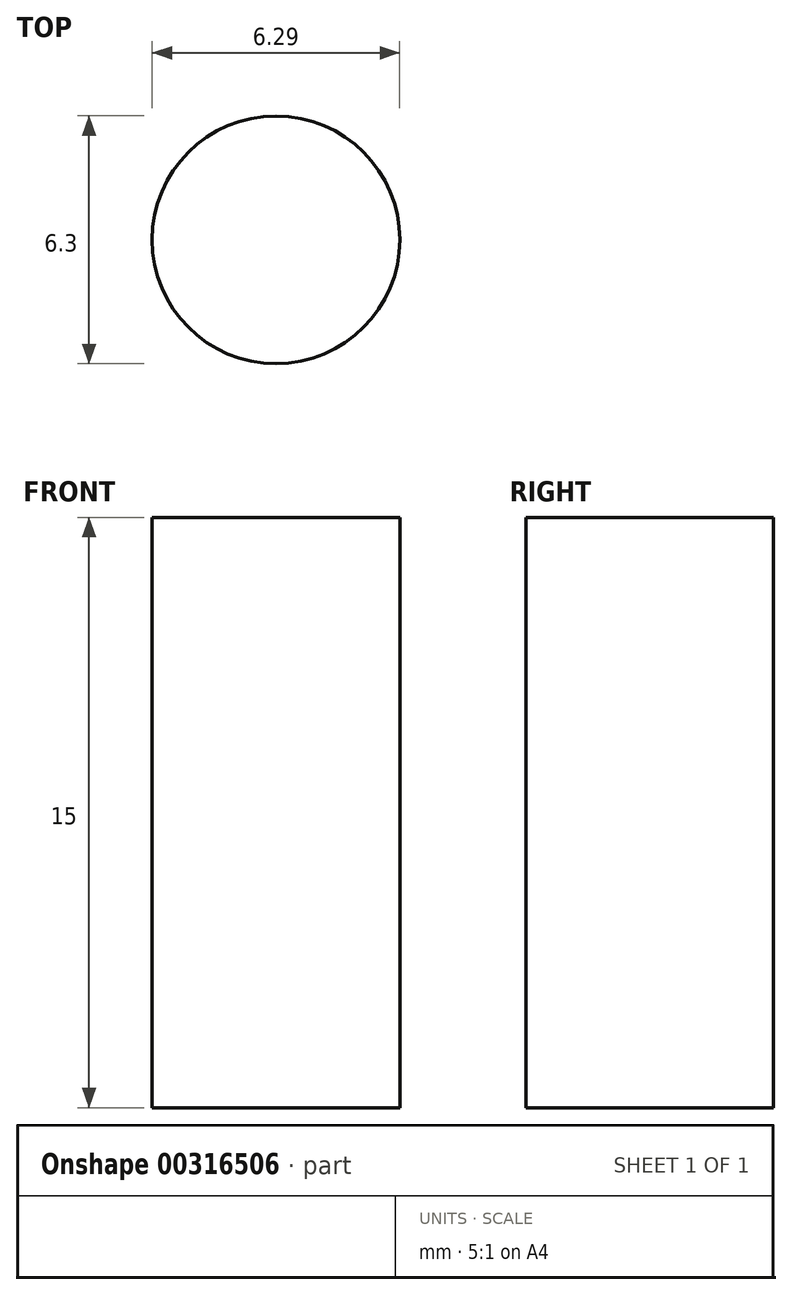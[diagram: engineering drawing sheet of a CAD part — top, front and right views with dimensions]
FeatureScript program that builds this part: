
annotation { "Feature Type Name" : "Feature", "Feature Type Description" : "" }
export const myFeature = defineFeature(function(context is Context, id is Id, definition is map)
    precondition{}
    {
        {
            var Q0;
            Q0=qCreatedBy(makeId("Top.planeOp"),FACE);
            var sketch = newSketch(context, id + "F0", { "sketchPlane" : qUnion([Q0])});
            skCircle(sketch, "E0", {"center": v(-40.26, 5.92) * mm, "radius": 3.15 * mm});
            skSolve(sketch);
        }
        {
            var Q0;
            Q0=makeQuery(id+"F0.imprint","IMPRINT",FACE,{"disambiguationData":[TD([[makeQuery(id+"F0.imprint","IMPRINT",EDGE,{"derivedFrom":sQuery(id+"F0.wireOp",EDGE,"E0")}),1.0]])]});
            extrude(context, id + "F1", {"entities" : qUnion([Q0]), "depth" : 15 * mm});
        }
    });
